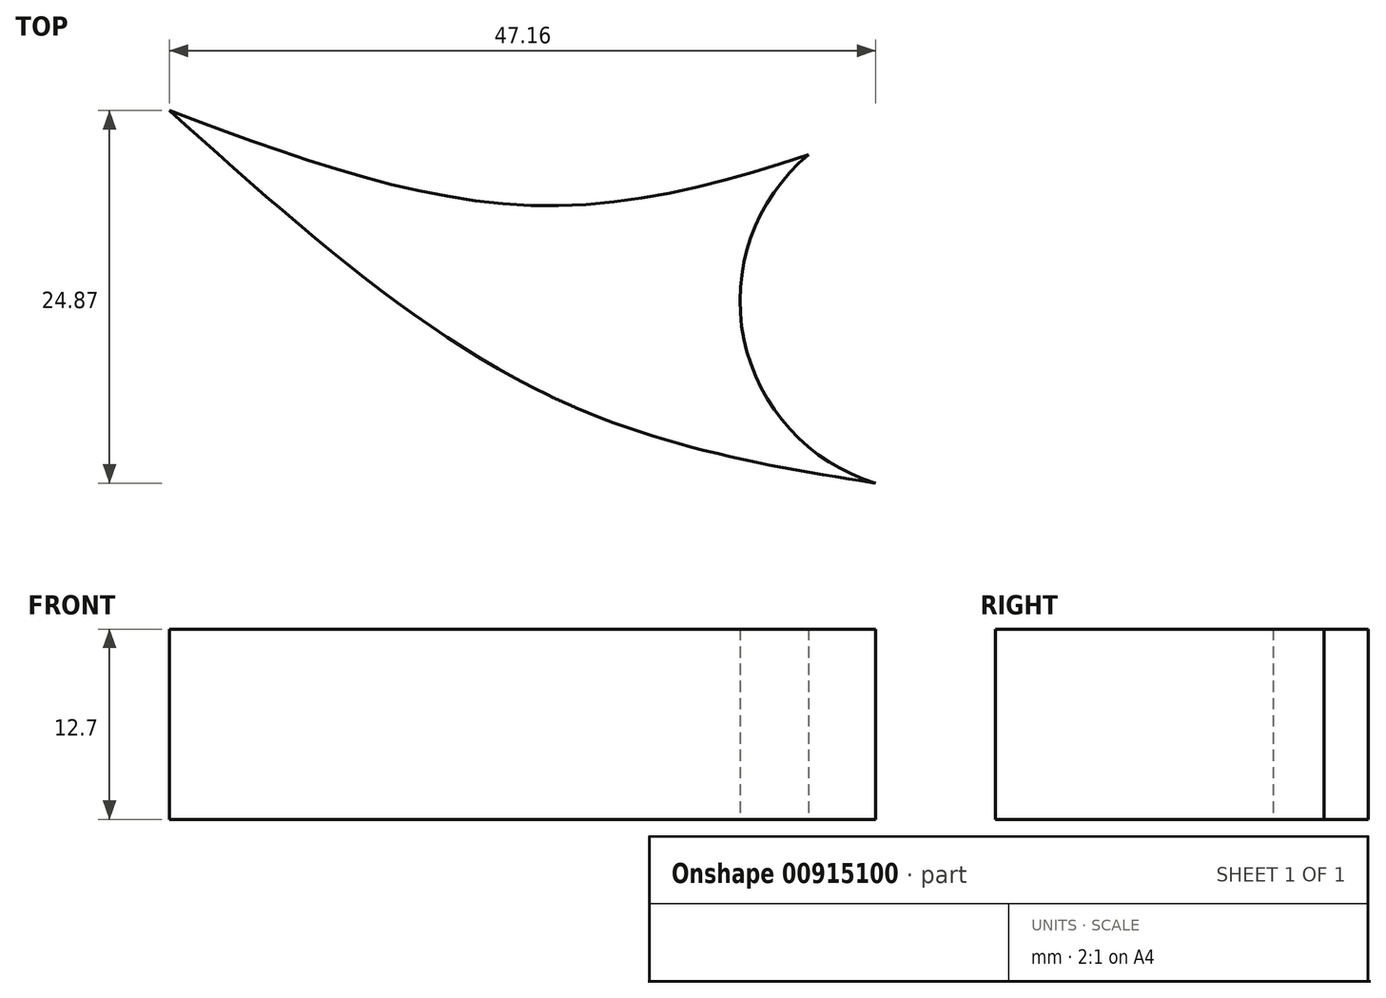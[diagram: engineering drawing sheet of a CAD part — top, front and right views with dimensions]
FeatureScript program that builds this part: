
annotation { "Feature Type Name" : "Feature", "Feature Type Description" : "" }
export const myFeature = defineFeature(function(context is Context, id is Id, definition is map)
    precondition{}
    {
        {
            var Q0;
            Q0=qCreatedBy(makeId("Top.planeOp"),FACE);
            var sketch = newSketch(context, id + "F0", { "sketchPlane" : qUnion([Q0])});
            skPoint(sketch, "E0.middle", {"position": v(0, 0) * mm});
            skFitSpline(sketch, "E1", {"points": [v(25.4, -12.7) * mm, v(0, -6.35) * mm, v(-25.4, 12.7) * mm], "startDerivative": vector(-59.23, 8.46) * mm, "endDerivative": vector(-42.38, 42.33) * mm});
            skFitSpline(sketch, "E2", {"points": [v(25.4, 12.7) * mm, v(0, 6.35) * mm, v(-25.4, 12.7) * mm], "startDerivative": vector(-50.8, -19.05) * mm, "endDerivative": vector(-50.8, 19.05) * mm});
            skPoint(sketch, "E3.orphan", {"position": v(0, 12.7) * mm});
            skPoint(sketch, "E4.orphan", {"position": v(-25.4, 0) * mm});
            skPoint(sketch, "E0.top.end.orphan", {"position": v(-25.4, -12.7) * mm});
            skFitSpline(sketch, "E5", {"points": [v(25.4, -12.7) * mm, v(0, -6.35) * mm, v(-25.4, 12.7) * mm], "startDerivative": vector(-54.54, 7.87) * mm, "endDerivative": vector(-47.18, 42.38) * mm});
            skArc(sketch, "E6", {"start": v(17.27, 9.75) * mm, "mid": v(12.96, -2.55) * mm, "end": v(21.76, -12.17) * mm});
            skSolve(sketch);
        }
        {
            var Q0;
            {var subQ0=sQuery(id+"F0.wireOp",EDGE,"E2");Q0=makeQuery(id+"F0.imprint","IMPRINT",FACE,{"disambiguationData":[TD([[makeQuery(id+"F0.imprint","IMPRINT",EDGE,{"derivedFrom":subQ0}),1.0]])]});}
            extrude(context, id + "F1", {"entities" : qUnion([Q0]), "depth" : 12.7 * mm, "offsetDistance" : 25.4 * mm});
        }
    });
